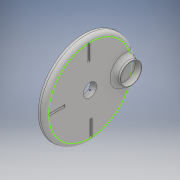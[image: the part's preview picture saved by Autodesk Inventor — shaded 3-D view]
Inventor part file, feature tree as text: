
AUTODESK INVENTOR PART (.ipt)
format: ipt  version: 2018 (Build 220112000, 112)  size: 453,632 bytes
history: native  units: mm
features: sketch x5, extrude x4, fillet x2
ambient origin geometry x8: Origin, YZ Plane, XZ Plane, XY Plane, X Axis, Y Axis, Z Axis, Center Point
bodies: Solid1 (feature_tree)
feature tree (11):
  extrude  "Extrusion1"  Depth=3.0mm TaperAngle=0.0deg
  extrude  "Extrusion2"  Depth=3.0mm TaperAngle=0.0deg
  fillet  "Fillet1"  Radius=2.0mm
  fillet  "Fillet2"  Radius=2.0mm
  extrude  "Extrusion3"  Depth=3.0mm TaperAngle=0.0deg
  sketch  "Sketch4"  dims[d11=8.0mm d12=1.0mm]
  extrude  "Extrusion4"  Depth=1.0mm
  sketch  "Sketch1"  dims[d0=44.45mm d1=3.0mm d2=0.0mm]
  sketch  "Sketch2"  dims[d3=10.0mm d4=3.0mm d5=0.0mm d6=2.0mm d7=2.0mm]
  sketch  "Sketch3"  dims[d8=6.5mm d9=3.0mm d10=0.0mm]
  sketch  "Sketch5"  dims[d13=1.0mm d14=8.0mm d15=8.0mm d16=1.0mm d17=2.0mm d18=0.0mm]
